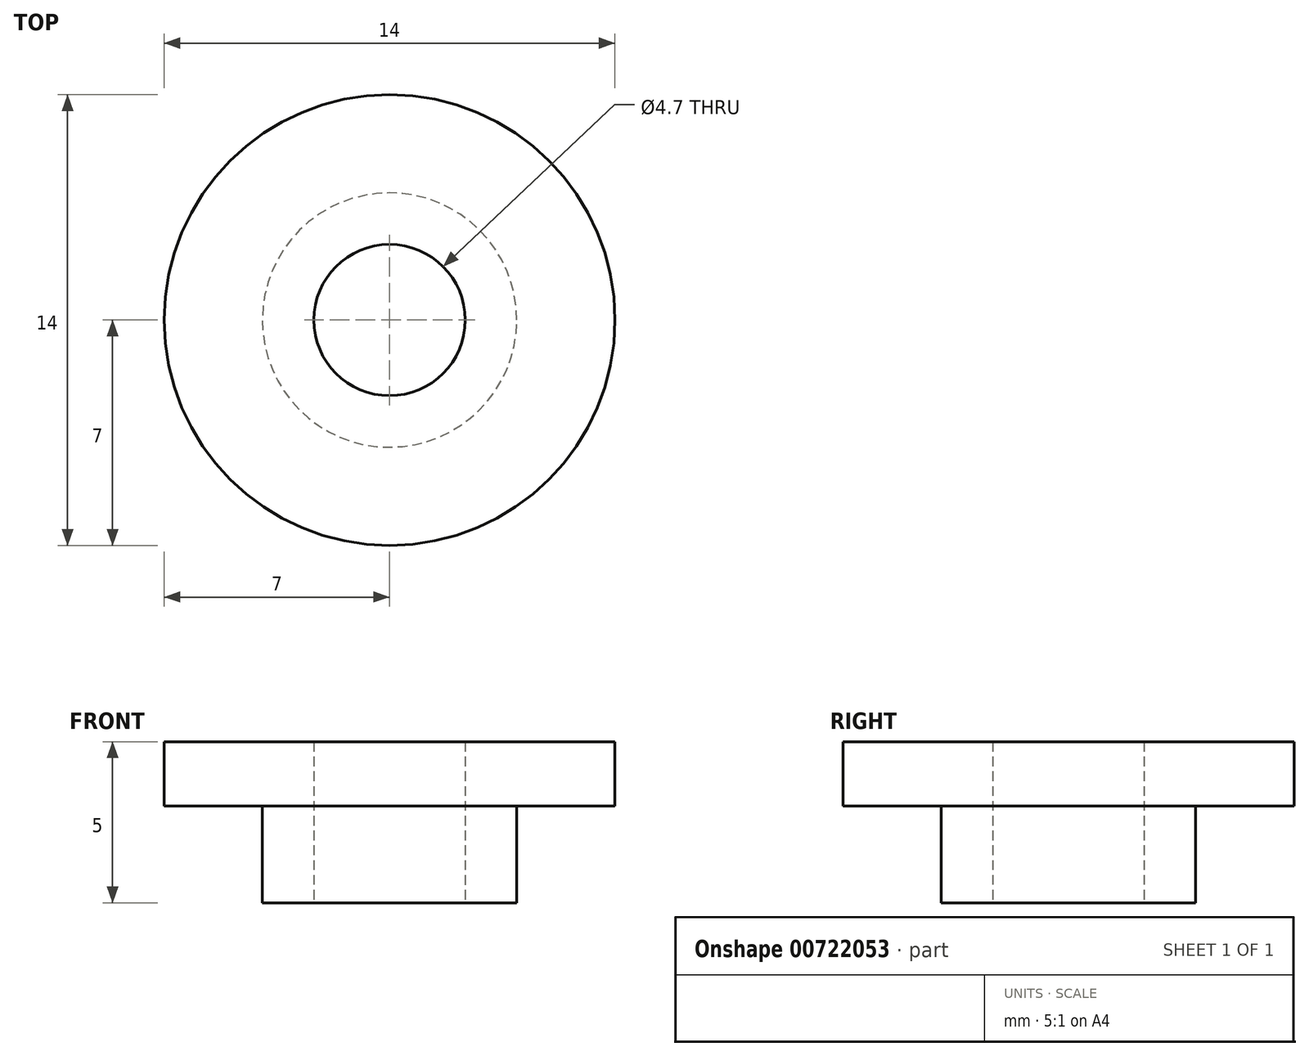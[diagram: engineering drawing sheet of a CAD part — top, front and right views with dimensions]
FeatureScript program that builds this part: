
annotation { "Feature Type Name" : "Feature", "Feature Type Description" : "" }
export const myFeature = defineFeature(function(context is Context, id is Id, definition is map)
    precondition{}
    {
        {
            var Q0;
            Q0=qCreatedBy(makeId("Top.planeOp"),FACE);
            var sketch = newSketch(context, id + "F0", { "sketchPlane" : qUnion([Q0])});
            skCircle(sketch, "E0", {"center": v(0, 0) * mm, "radius": 7 * mm});
            skCircle(sketch, "E1", {"center": v(0, 0) * mm, "radius": 2.35 * mm});
            skSolve(sketch);
        }
        {
            var Q0;
            Q0 = qSketchRegion(id + "F0", true);
            extrude(context, id + "F1", {"entities" : qUnion([Q0]), "depth" : 2 * mm, "offsetDistance" : 25 * mm});
        }
        {
            var Q0;
            Q0=makeQuery(id+"F1.opExtrude","CAP_FACE",FACE,{"disambiguationData":[OSD([sQuery(id+"F0.wireOp",EDGE,"E0"),sQuery(id+"F0.wireOp",EDGE,"E1")])],"isStart":true});
            var sketch = newSketch(context, id + "F2", { "sketchPlane" : qUnion([Q0])});
            skCircle(sketch, "E2", {"center": v(0, 0) * mm, "radius": 3.95 * mm});
            skCircle(sketch, "E3.0", {"center": v(0, 0) * mm, "radius": 2.35 * mm});
            skSolve(sketch);
        }
        {
            var Q0;
            Q0 = qSketchRegion(id + "F2", true);
            extrude(context, id + "F3", {"entities" : qUnion([Q0]), "operationType" : NewBodyOperationType.ADD, "depth" : 3 * mm, "offsetDistance" : 25 * mm});
        }
    });
